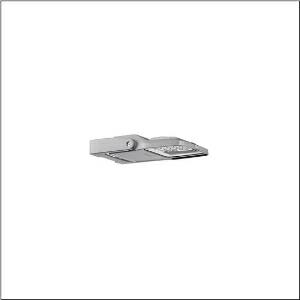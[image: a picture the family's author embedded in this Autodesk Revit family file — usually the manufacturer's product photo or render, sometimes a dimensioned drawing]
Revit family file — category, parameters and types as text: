
# Revit family: floodlight_fl_21_iq_micro___pl52_5xa7761a4d2a_29c7
name_source: partatom
category: Lighting Fixtures
units: mm (PartAtom-declared; Revit-internal decimal feet)

## family parameters
Cut with Voids When Loaded = No
Host = Face
Light Source = No
Part Type = Normal
Room Calculation Point = No
Round Connector Dimension = Use Diameter
Shared = No

## types (1)
- --- (1 x LED, 3010 lm, 23.1 W, 4000K)
    Apparent Load = 23 VA
    CIE Flux Codes = 26 60 98 100 100
    Color Rendering = 70
    Color Temperature = 4000K
    Default Elevation = 1800 mm
    Description = Floodlight FL 21 iQ micro, floodlight, primary light control with lens, of PMMA, primary optical cover: protective disc, of toughened safety glass, transparent, light distribution: PL52, light emission: direct distribution, installation type: surface-mounted, LED, High Power LED, rated luminous flux: 3.010lm, luminous efficacy: 130lm/W, light colour: 740, colour temperature: 4000K, control gear: iQ Comfort/DALI, control: optimised constant luminous flux control (CLO 2.0), Desk-Remote (wireless, voltage-free reading and setting of iQ features in the workshop via application-optimized NFC function/RFID function), Light-Fading, Smart-Wire, Night-Set, Lumen-Switch, Temp-Guard, Auto-Match, with terminal, 6-pole, mains connection: 220..240V, AC, 50/60Hz, start of lifetime: 23W, end of service life: 24W, reduction: 11W, luminaire housing, of diecast aluminium, powder-coated, Siteco® metallic grey (DB 702S), corrosivity category C5 mid according to DIN EN ISO 12944, suitable for swimming pools, chlorine-resistant, sealing non-destructively replaceable, design bracket, of diecast aluminium, powder-coated, Siteco® metallic grey (DB 702S), protection rating (complete): IP66, insulation class (complete): insulation class II (safety insulation), certification: CE, ENEC, VDE, protection symbol: D, impact resistance: IK07, permissible operating ambient temperature: -40..+40°C, permissible operating ambient temperature for outdoor applications: -40..+50°C, standard: DIN EN 12944, LABS conformity tested according to VDMA 24364:2018-05, packaging unit: 1 piece

Light Distribution: PL52
    Height = 65 mm
    Lamp = 1 x LED
    Lamp Light Flux = 3010 lm
    Lamp Power = 23.1 W
    Lamp count = 1
    Length = 312 mm
    Luminous efficacy = 130 lm/W
    Manufacturer = Siteco
    ModVariant = No
    Model = 5XA7761A4D2A
    Mounting Place = Wall
    Mounting Type = Surface mounted
    Number of Poles = 1
    OnlyDefault = Yes
    Power Factor = 1
    Product Name = Floodlight FL 21 iQ micro | PL52
    Product group = floodlight | wall mounted
    ProductGroupID = 2001
    Protection Class = Protection class II
    Protection Degree = IP 66
    RLX_Detail_Level = 1
    RLX_Emergency_Light_Flux = 0 lm
    RLX_Emergency_Type = 0
    RLX_Emergency_Type_DB = No
    RlxData = <blob elided: 97705 chars, md5=56fe9156>
    Socket = socket
    Standby Power = 0 W
    System Light Flux = 3010 lm
    System Power = 23 W
    Type Comments = factory setting: luminous flux: 100 % | dim-lin: 254 | 455 mA
    Type Image = l_1006878.jpg
    URL = http://relux.com
    VarID = @adj_178026
    Voltage = 0 V
    Weight = 0.00 kg
    Width = 230 mm

## geometry (parser evidence)
native form markers: Blend x4, Sweep x13
no freeform markers — native parametric forms only
